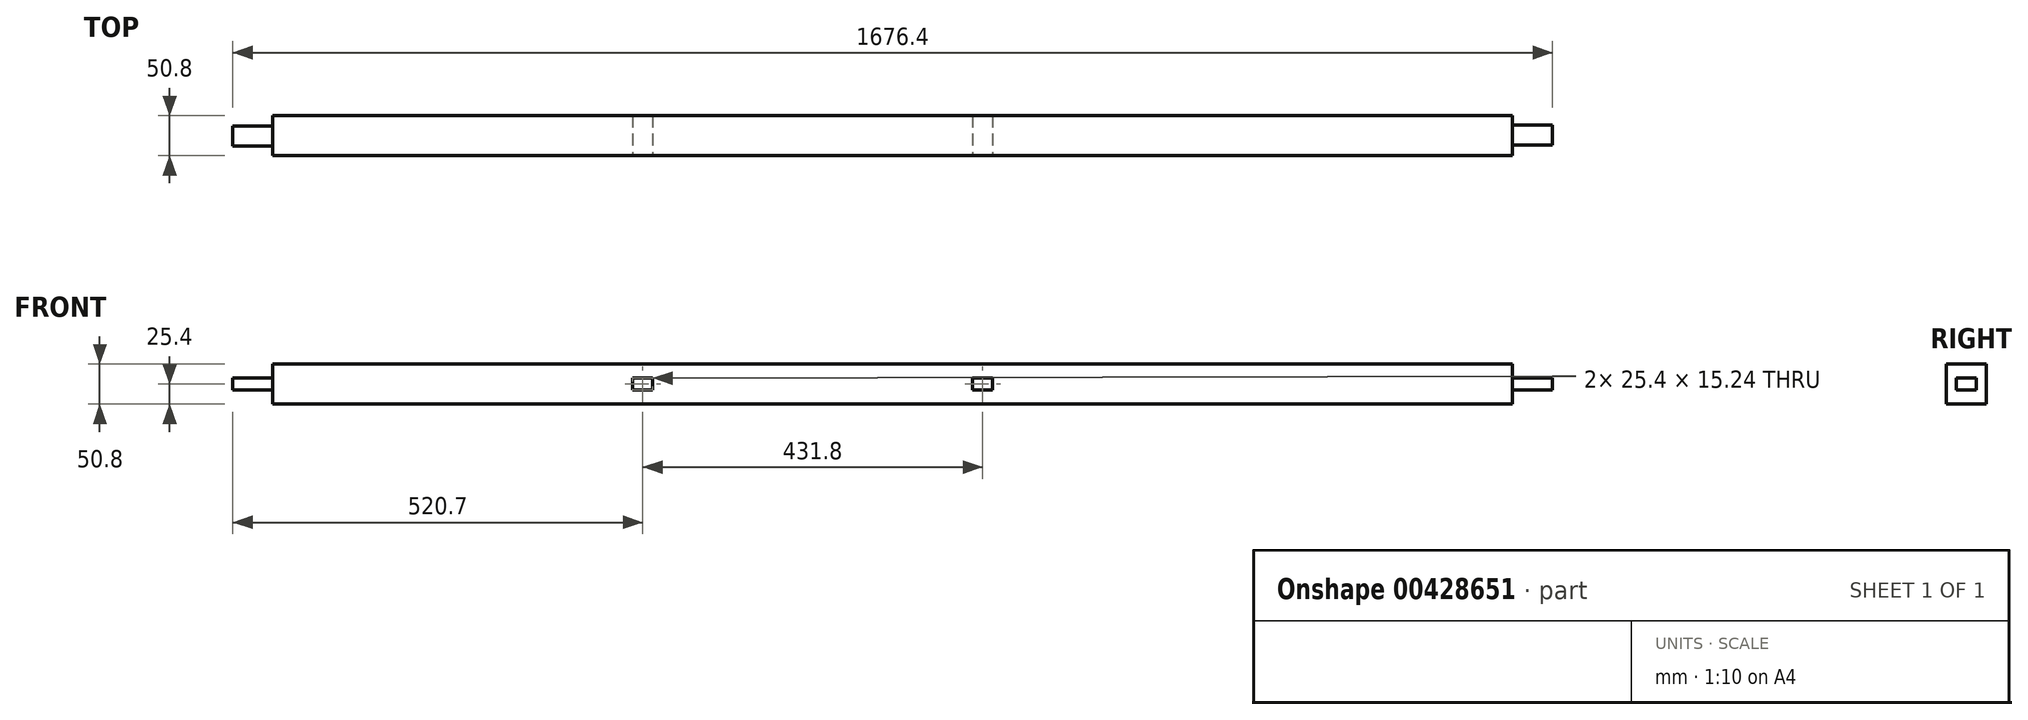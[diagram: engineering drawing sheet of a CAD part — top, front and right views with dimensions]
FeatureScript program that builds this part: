
annotation { "Feature Type Name" : "Feature", "Feature Type Description" : "" }
export const myFeature = defineFeature(function(context is Context, id is Id, definition is map)
    precondition{}
    {
        {
            var Q0;
            Q0=qCreatedBy(makeId("Top.planeOp"),FACE);
            var sketch = newSketch(context, id + "F0", { "sketchPlane" : qUnion([Q0])});
            skLineSegment(sketch, "E0.bottom", {"start": v(-838.2, 25.4) * mm, "end": v(838.2, 25.4) * mm});
            skLineSegment(sketch, "E0.top", {"start": v(-838.2, -25.4) * mm, "end": v(838.2, -25.4) * mm});
            skLineSegment(sketch, "E0.left", {"start": v(-838.2, 25.4) * mm, "end": v(-838.2, -25.4) * mm});
            skLineSegment(sketch, "E0.right", {"start": v(838.2, 25.4) * mm, "end": v(838.2, -25.4) * mm});
            skPoint(sketch, "E0.middle", {"position": v(0, 0) * mm});
            skSolve(sketch);
        }
        {
            var Q0;
            Q0 = qSketchRegion(id + "F0", true);
            extrude(context, id + "F1", {"entities" : qUnion([Q0]), "depth" : 50.8 * mm});
        }
        {
            var Q0;
            Q0=makeQuery(id+"F1.opExtrude","SWEPT_FACE",FACE,{"disambiguationData":[OSD([sQuery(id+"F0.wireOp",EDGE,"E0.left")])]});
            var sketch = newSketch(context, id + "F2", { "sketchPlane" : qUnion([Q0])});
            skLineSegment(sketch, "E1", {"start": v(-25.4, 50.8) * mm, "end": v(-25.4, 0) * mm});
            skLineSegment(sketch, "E2", {"start": v(-25.4, 0) * mm, "end": v(25.4, 0) * mm});
            skLineSegment(sketch, "E3", {"start": v(25.4, 0) * mm, "end": v(25.4, 50.8) * mm});
            skLineSegment(sketch, "E4", {"start": v(25.4, 50.8) * mm, "end": v(-25.4, 50.8) * mm});
            skPoint(sketch, "E5.endSnap0", {"position": v(0, 50.8) * mm});
            skLineSegment(sketch, "E6", {"start": v(0, 33.02) * mm, "end": v(-12.18, 33.02) * mm});
            skLineSegment(sketch, "E7", {"start": v(-12.18, 33.02) * mm, "end": v(-12.18, 17.78) * mm});
            skLineSegment(sketch, "E8", {"start": v(-12.18, 17.78) * mm, "end": v(13.22, 17.78) * mm});
            skLineSegment(sketch, "E9", {"start": v(13.22, 17.78) * mm, "end": v(13.22, 33.02) * mm});
            skLineSegment(sketch, "E10", {"start": v(13.22, 33.02) * mm, "end": v(0, 33.02) * mm});
            skSolve(sketch);
        }
        {
            var Q0;
            Q0 = qSketchRegion(id + "F2", true);
            extrude(context, id + "F3", {"entities" : qUnion([Q0]), "operationType" : NewBodyOperationType.REMOVE, "oppositeDirection" : true, "depth" : 50.8 * mm});
        }
        {
            var Q0;
            Q0=makeQuery(id+"F1.opExtrude","SWEPT_FACE",FACE,{"disambiguationData":[OSD([sQuery(id+"F0.wireOp",EDGE,"E0.right")])]});
            var sketch = newSketch(context, id + "F4", { "sketchPlane" : qUnion([Q0])});
            skPoint(sketch, "E11.endSnap0", {"position": v(0, 50.8) * mm});
            skLineSegment(sketch, "E12", {"start": v(0, 33.02) * mm, "end": v(-12.18, 33.02) * mm});
            skLineSegment(sketch, "E13", {"start": v(-12.18, 33.02) * mm, "end": v(-12.18, 17.78) * mm});
            skLineSegment(sketch, "E14", {"start": v(-12.18, 17.78) * mm, "end": v(13.22, 17.78) * mm});
            skLineSegment(sketch, "E15", {"start": v(13.22, 17.78) * mm, "end": v(13.22, 33.02) * mm});
            skLineSegment(sketch, "E16", {"start": v(13.22, 33.02) * mm, "end": v(0, 33.02) * mm});
            skLineSegment(sketch, "E17", {"start": v(0, 50.8) * mm, "end": v(-25.4, 50.8) * mm});
            skLineSegment(sketch, "E18", {"start": v(-25.4, 50.8) * mm, "end": v(-25.4, 0) * mm});
            skLineSegment(sketch, "E19", {"start": v(-25.4, 0) * mm, "end": v(25.4, 0) * mm});
            skLineSegment(sketch, "E20", {"start": v(25.4, 0) * mm, "end": v(25.4, 50.8) * mm});
            skLineSegment(sketch, "E21", {"start": v(25.4, 50.8) * mm, "end": v(-25.4, 50.8) * mm});
            skSolve(sketch);
        }
        {
            var Q0;
            Q0 = qSketchRegion(id + "F4", true);
            extrude(context, id + "F5", {"entities" : qUnion([Q0]), "operationType" : NewBodyOperationType.REMOVE, "oppositeDirection" : true, "depth" : 50.8 * mm});
        }
        {
            var Q0;
            Q0=makeQuery(id+"F1.opExtrude","SWEPT_FACE",FACE,{"disambiguationData":[OSD([sQuery(id+"F0.wireOp",EDGE,"E0.top")])]});
            var sketch = newSketch(context, id + "F6", { "sketchPlane" : qUnion([Q0])});
            skLineSegment(sketch, "E22.bottom", {"start": v(-330.2, 17.78) * mm, "end": v(-304.8, 17.78) * mm});
            skLineSegment(sketch, "E22.top", {"start": v(-330.2, 33.02) * mm, "end": v(-304.8, 33.02) * mm});
            skLineSegment(sketch, "E22.left", {"start": v(-330.2, 17.78) * mm, "end": v(-330.2, 33.02) * mm});
            skLineSegment(sketch, "E22.right", {"start": v(-304.8, 17.78) * mm, "end": v(-304.8, 33.02) * mm});
            skSolve(sketch);
        }
        {
            var Q0;
            Q0 = qSketchRegion(id + "F6", true);
            extrude(context, id + "F7", {"entities" : qUnion([Q0]), "operationType" : NewBodyOperationType.REMOVE, "oppositeDirection" : true, "depth" : 50.8 * mm});
        }
        {
            var Q0;
            Q0=makeQuery(id+"F1.opExtrude","SWEPT_FACE",FACE,{"disambiguationData":[OSD([sQuery(id+"F0.wireOp",EDGE,"E0.top")])]});
            var sketch = newSketch(context, id + "F8", { "sketchPlane" : qUnion([Q0])});
            skLineSegment(sketch, "E23.bottom", {"start": v(127, 17.78) * mm, "end": v(101.6, 17.78) * mm});
            skLineSegment(sketch, "E23.top", {"start": v(127, 33.02) * mm, "end": v(101.6, 33.02) * mm});
            skLineSegment(sketch, "E23.right", {"start": v(101.6, 17.78) * mm, "end": v(101.6, 33.02) * mm});
            skLineSegment(sketch, "E24", {"start": v(127, 33.02) * mm, "end": v(127, 17.78) * mm});
            skSolve(sketch);
        }
        {
            var Q0;
            Q0 = qSketchRegion(id + "F8", true);
            extrude(context, id + "F9", {"entities" : qUnion([Q0]), "operationType" : NewBodyOperationType.REMOVE, "oppositeDirection" : true, "depth" : 50.8 * mm});
        }
    });
